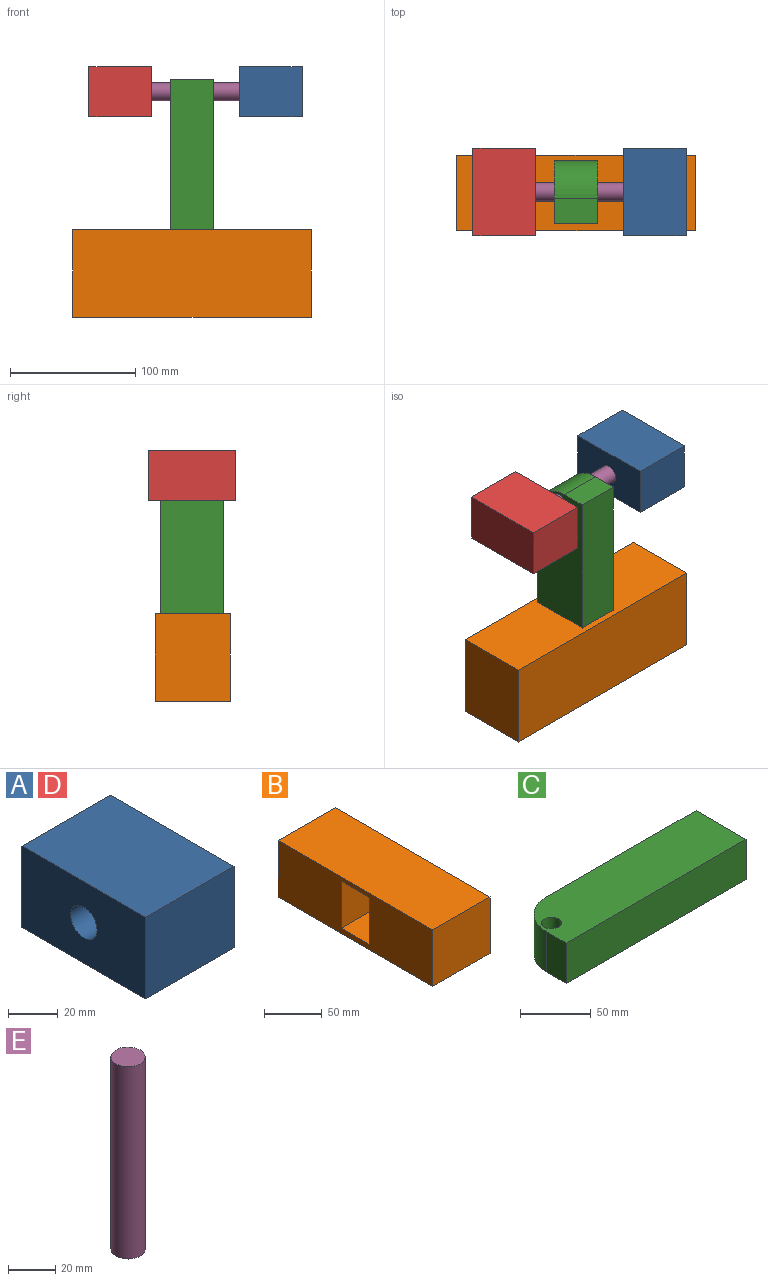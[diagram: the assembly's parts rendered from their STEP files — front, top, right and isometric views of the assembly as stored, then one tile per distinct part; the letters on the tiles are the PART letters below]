
ASSEMBLY  parts=5 mates=6
PART A: 8 faces, bbox 50x70x40 mm
  f0: plane 50x40mm, normal (0,1,0), area 2000mm2, adj f1,f3,f4,f5
  f1: plane 70x40mm, normal (-1,0,0), area 2623.3mm2, adj f0,f2,f4,f5,f6
  f2: plane 50x40mm, normal (0,-1,0), area 2000mm2, adj f1,f3,f4,f5
  f3: plane 70x40mm, normal (1,0,0), area 2800mm2, adj f0,f2,f4,f5
  f4: plane 70x50mm, normal (0,0,1), area 3500mm2, adj f0,f1,f2,f3
  f5: plane 70x50mm, normal (0,0,-1), area 3500mm2, adj f0,f1,f2,f3
  f6: cylinder r=7.5mm len=15mm, axis (-1,0,0), area 706.9mm2, adj f1,f7
  f7: plane 15x15mm, normal (-1,0,0), area 176.7mm2, adj f6
PART B: 11 faces, bbox 70x190x60 mm
  f0: plane 190x60mm, normal (-1,0,0), area 9650mm2, adj f1,f2,f4,f5,f6,f7,f8,f9
  f1: plane 70x60mm, normal (0,1,0), area 4200mm2, adj f0,f3,f4,f5
  f2: plane 70x60mm, normal (0,-1,0), area 4200mm2, adj f0,f3,f4,f5
  f3: plane 190x60mm, normal (1,0,0), area 11400mm2, adj f1,f2,f4,f5
  f4: plane 190x70mm, normal (0,0,1), area 13300mm2, adj f0,f1,f2,f3
  f5: plane 190x70mm, normal (0,0,-1), area 13300mm2, adj f0,f1,f2,f3
  f6: plane 60x50mm, normal (0,-1,0), area 3000mm2, adj f0,f7,f9,f10
  f7: plane 60x35mm, normal (0,0,1), area 2100mm2, adj f0,f6,f8,f10
  f8: plane 60x50mm, normal (0,1,0), area 3000mm2, adj f0,f7,f9,f10
  f9: plane 60x35mm, normal (0,0,-1), area 2100mm2, adj f0,f6,f8,f10
  f10: plane 50x35mm, normal (-1,0,0), area 1750mm2, adj f6,f7,f8,f9
PART C: 8 faces, bbox 180x50x35 mm
  f0: plane 150x35mm, normal (0,1,0), area 5250mm2, adj f3,f4,f5,f7
  f1: plane 35x20mm, normal (-1,0,0), area 700mm2, adj f2,f4,f5,f7
  f2: plane 180x35mm, normal (0,-1,0), area 6300mm2, adj f1,f3,f4,f5
  f3: plane 50x35mm, normal (1,0,0), area 1750mm2, adj f0,f2,f4,f5
  f4: plane 180x50mm, normal (0,0,1), area 8652.9mm2, adj f0,f1,f2,f3,f6,f7
  f5: plane 180x50mm, normal (0,0,-1), area 8652.9mm2, adj f0,f1,f2,f3,f6,f7
  f6: cylinder r=7mm len=35mm, axis (0,0,1), area 1539.4mm2, adj f4,f5
  f7: cylinder r=30mm len=35mm, axis (0,0,1), area 1649.3mm2, adj f0,f1,f4,f5
PART D: same geometry as A
PART E: 3 faces, bbox 14.5x14.5x100 mm
  f0: cylinder r=7.25mm len=100mm, axis (0,0,-1), area 4555.3mm2, adj f1,f2
  f1: plane 14.5x14.5mm, normal (0,0,1), area 165.1mm2, adj f0
  f2: plane 14.5x14.5mm, normal (0,0,-1), area 165.1mm2, adj f0
PLACE A rot(axis=(0,-1,0.04),0deg) t=(8.62,-8.92,-17.77)mm
PLACE B rot(axis=(-0.58,0.58,0.58),120deg) t=(-54.19,-39.52,-142.77)mm
PLACE C rot(axis=(0,1,0),90deg) t=(-71.69,-8.92,-77.77)mm
PLACE D rot(axis=(0,0,1),180deg) t=(-111.38,-8.92,-17.77)mm
PLACE E rot(axis=(0,-1,0),90deg) t=(-1.38,-8.92,2.23)mm
MATE slider C.f6 <-> E.f0  axis (-1,0,0) through (-71.69,-8.92,2.23)mm
MATE fastened A.f6 <-> E.f0  axis (-1,0,0) through (-1.38,-8.92,2.23)mm
MATE slider E.f0 <-> A.f6  axis (1,0,0) through (-1.38,-8.92,2.23)mm
MATE fastened B.f10 <-> C.f3  axis (0,0,1) through (-54.19,-8.92,-167.77)mm
MATE fastened D.f6 <-> E.f0  axis (1,0,0) through (-101.38,-8.92,2.23)mm
MATE slider E.f0 <-> D.f6  axis (1,0,0) through (-101.38,-8.92,2.23)mm
